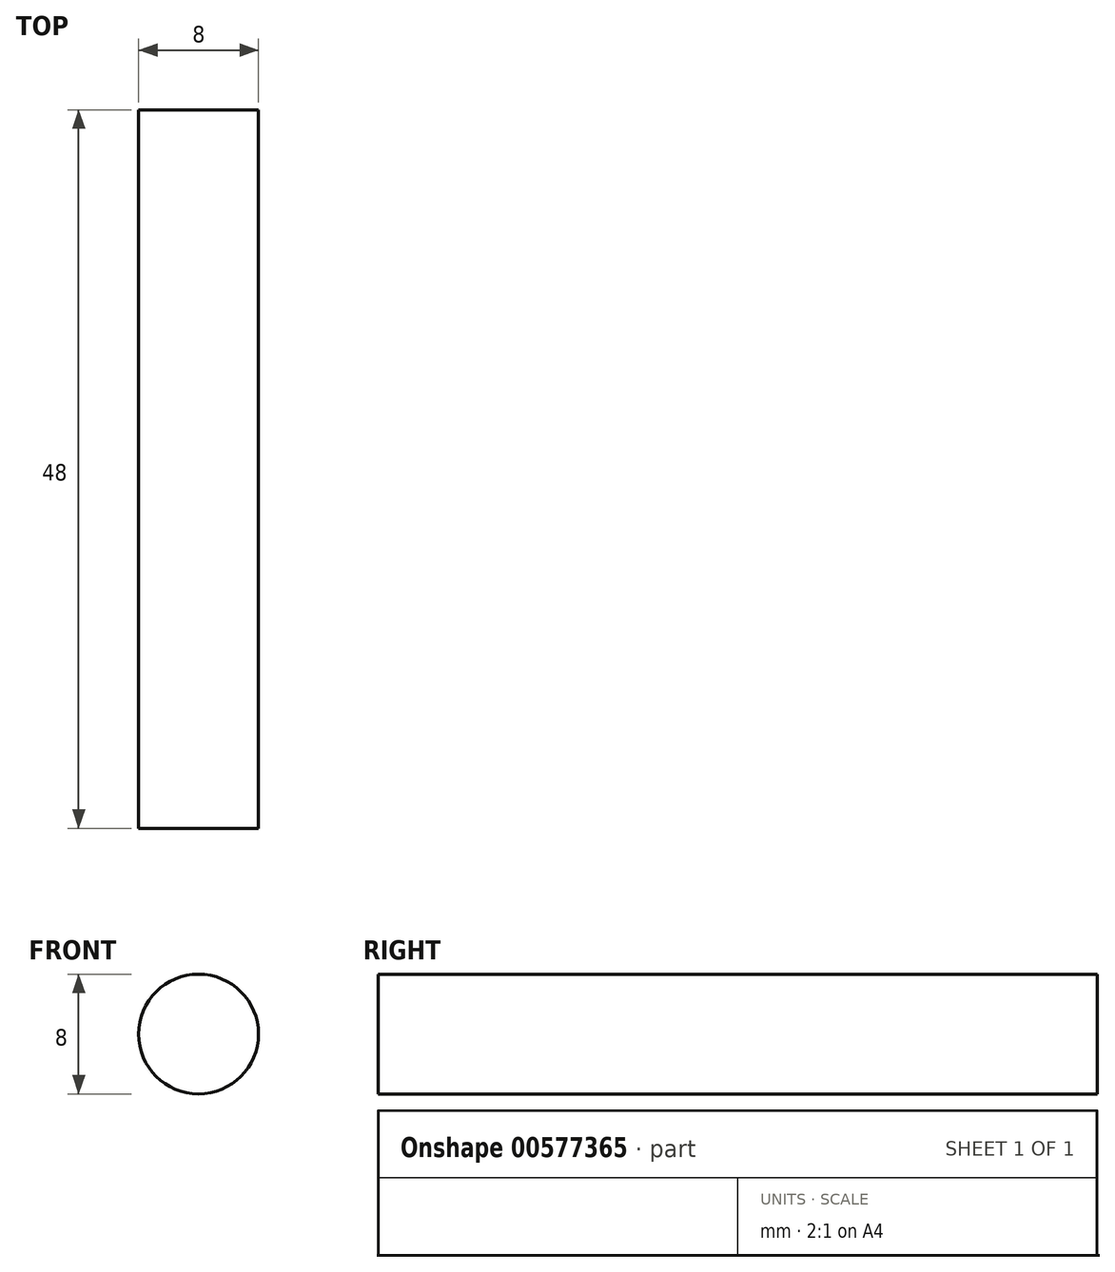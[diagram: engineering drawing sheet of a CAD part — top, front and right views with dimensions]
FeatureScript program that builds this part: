
annotation { "Feature Type Name" : "Feature", "Feature Type Description" : "" }
export const myFeature = defineFeature(function(context is Context, id is Id, definition is map)
    precondition{}
    {
        {
            var Q0;
            Q0=qCreatedBy(makeId("Front.planeOp"),FACE);
            var sketch = newSketch(context, id + "F0", { "sketchPlane" : qUnion([Q0])});
            skCircle(sketch, "E0", {"center": v(0, 0) * mm, "radius": 4 * mm});
            skSolve(sketch);
        }
        {
            var Q0;
            Q0=qSketchRegion(id+"F0",true);
            extrude(context, id + "F1", {"entities" : qUnion([Q0]), "depth" : 48 * mm, "offsetDistance" : 25 * mm});
        }
    });
